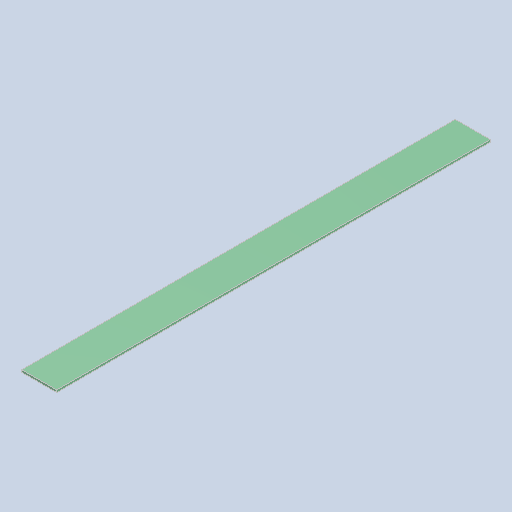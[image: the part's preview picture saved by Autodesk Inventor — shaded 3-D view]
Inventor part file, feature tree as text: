
AUTODESK INVENTOR PART (.ipt)
format: ipt  version: 2022 (Build 260153000, 153)  size: 95,744 bytes
history: native  units: mm
features: other x1, extrude x1, sketch x1
ambient origin geometry x8: Origin, YZ Plane, XZ Plane, XY Plane, X Axis, Y Axis, Z Axis, Center Point
bodies: Body1 (feature_tree)
feature tree (3):
  other  "ソリッド1"
  extrude  "押し出し1"  Depth=360.0mm
  sketch  "スケッチ1"
